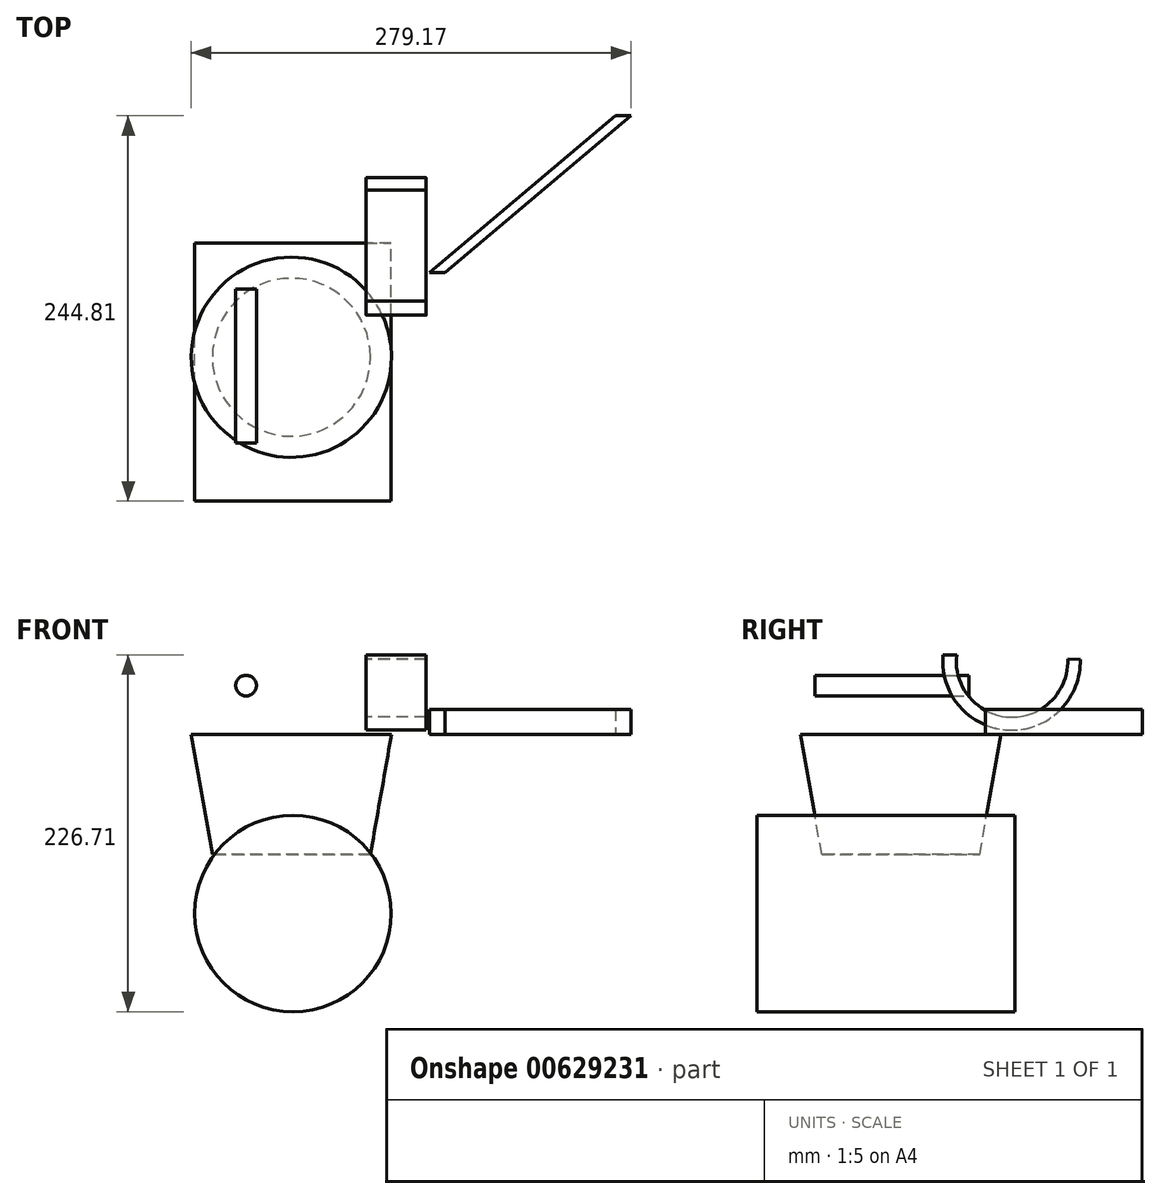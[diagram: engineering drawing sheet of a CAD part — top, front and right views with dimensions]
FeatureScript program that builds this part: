
annotation { "Feature Type Name" : "Feature", "Feature Type Description" : "" }
export const myFeature = defineFeature(function(context is Context, id is Id, definition is map)
    precondition{}
    {
        {
            var Q0;
            Q0=qCreatedBy(makeId("Top.planeOp"),FACE);
            var sketch = newSketch(context, id + "F0", { "sketchPlane" : qUnion([Q0])});
            skCircle(sketch, "E0", {"center": v(-47.57, -35.54) * mm, "radius": 63.6 * mm});
            skSolve(sketch);
        }
        {
            var Q0;
            Q0=makeQuery(id+"F0.imprint","IMPRINT",FACE,{"disambiguationData":[TD([[makeQuery(id+"F0.imprint","IMPRINT",EDGE,{"derivedFrom":sQuery(id+"F0.wireOp",EDGE,"E0")}),1.0]])]});
            extrude(context, id + "F1", {"entities" : qUnion([Q0]), "oppositeDirection" : true, "depth" : 76.2 * mm, "offsetDistance" : 25.4 * mm, "hasDraft" : true, "draftAngle" : 10 * degree, "draftPullDirection" : true});
        }
        {
            var Q0;
            Q0=qCreatedBy(makeId("Front.planeOp"),FACE);
            var sketch = newSketch(context, id + "F2", { "sketchPlane" : qUnion([Q0])});
            skCircle(sketch, "E1", {"center": v(-46.55, -113.64) * mm, "radius": 62.36 * mm});
            skSolve(sketch);
        }
        {
            var Q0;
            Q0=makeQuery(id+"F2.imprint","IMPRINT",FACE,{"disambiguationData":[TD([[makeQuery(id+"F2.imprint","IMPRINT",EDGE,{"derivedFrom":sQuery(id+"F2.wireOp",EDGE,"E1")}),1.0]])]});
            extrude(context, id + "F3", {"entities" : qUnion([Q0]), "depth" : 127 * mm, "offsetDistance" : 25.4 * mm, "hasSecondDirection" : true, "secondDirectionOppositeDirection" : true, "secondDirectionDepth" : 37.08 * mm});
        }
        {
            var Q0;
            Q0=qCreatedBy(makeId("Front.planeOp"),FACE);
            var sketch = newSketch(context, id + "F4", { "sketchPlane" : qUnion([Q0])});
            skCircle(sketch, "E2", {"center": v(-76.34, 31.1) * mm, "radius": 6.56 * mm});
            skSolve(sketch);
        }
        {
            var Q0;
            Q0=makeQuery(id+"F4.imprint","IMPRINT",FACE,{"disambiguationData":[TD([[makeQuery(id+"F4.imprint","IMPRINT",EDGE,{"derivedFrom":sQuery(id+"F4.wireOp",EDGE,"E2")}),1.0]])]});
            var Q1;
            Q1=sQuery(id+"F4.wireOp",EDGE,"E2");
            extrude(context, id + "F5", {"entities" : qUnion([Q0]), "surfaceEntities" : qUnion([Q1]), "depth" : 89.92 * mm, "offsetDistance" : 25.4 * mm, "hasSecondDirection" : true, "secondDirectionOppositeDirection" : true, "secondDirectionDepth" : 7.62 * mm});
        }
        {
            var Q0;
            Q0=qCreatedBy(makeId("Top.planeOp"),FACE);
            var sketch = newSketch(context, id + "F6", { "sketchPlane" : qUnion([Q0])});
            skLineSegment(sketch, "E3", {"start": v(49.87, 18.17) * mm, "end": v(168, 117.81) * mm});
            skLineSegment(sketch, "E4", {"start": v(40.1, 18.17) * mm, "end": v(158.23, 117.81) * mm});
            skLineSegment(sketch, "E5", {"start": v(158.23, 117.81) * mm, "end": v(168, 117.81) * mm});
            skLineSegment(sketch, "E6", {"start": v(49.87, 18.17) * mm, "end": v(40.1, 18.17) * mm});
            skSolve(sketch);
        }
        {
            var Q0;
            Q0=makeQuery(id+"F6.imprint","IMPRINT",FACE,{"disambiguationData":[TD([[makeQuery(id+"F6.imprint","IMPRINT",EDGE,{"derivedFrom":sQuery(id+"F6.wireOp",EDGE,"E3")}),1.0]])]});
            var Q1;
            Q1=sQuery(id+"F6.wireOp",EDGE,"E5");
            var Q2;
            Q2=sQuery(id+"F6.wireOp",EDGE,"E6");
            var Q3;
            Q3=sQuery(id+"F6.wireOp",EDGE,"E3");
            var Q4;
            Q4=sQuery(id+"F6.wireOp",EDGE,"E4");
            extrude(context, id + "F7", {"entities" : qUnion([Q0]), "surfaceEntities" : qUnion([Q1, Q2, Q3, Q4]), "depth" : 16 * mm, "offsetDistance" : 25.4 * mm});
        }
        {
            var Q0;
            Q0=qCreatedBy(makeId("Right.planeOp"),FACE);
            var sketch = newSketch(context, id + "F8", { "sketchPlane" : qUnion([Q0])});
            skArc(sketch, "E7", {"start": v(0, 50.7) * mm, "mid": v(33.78, 11.12) * mm, "end": v(70.54, 47.96) * mm});
            skArc(sketch, "E8", {"start": v(-8.62, 50.7) * mm, "mid": v(33.38, 2.85) * mm, "end": v(78.45, 47.82) * mm});
            skLineSegment(sketch, "E9", {"start": v(-8.62, 50.7) * mm, "end": v(0, 50.7) * mm});
            skLineSegment(sketch, "E10", {"start": v(70.54, 47.96) * mm, "end": v(78.45, 47.82) * mm});
            skSolve(sketch);
        }
        {
            var Q0;
            Q0=makeQuery(id+"F8.imprint","IMPRINT",FACE,{"disambiguationData":[TD([[makeQuery(id+"F8.imprint","IMPRINT",EDGE,{"derivedFrom":sQuery(id+"F8.wireOp",EDGE,"E7")}),-1.0]])]});
            extrude(context, id + "F9", {"entities" : qUnion([Q0]), "depth" : 38.1 * mm, "offsetDistance" : 25.4 * mm});
        }
    });
